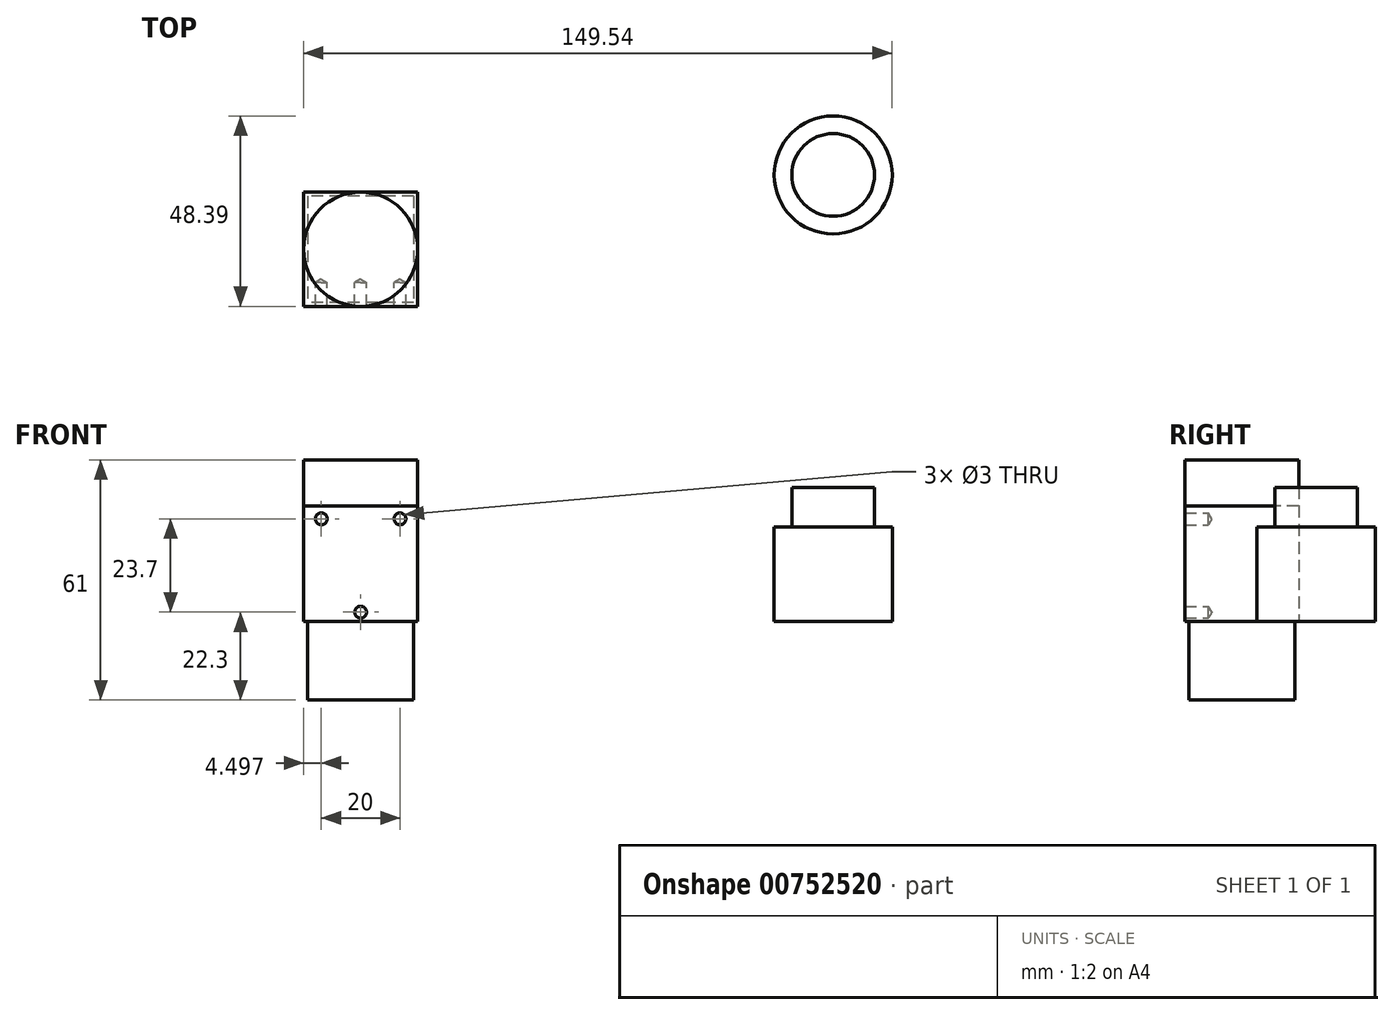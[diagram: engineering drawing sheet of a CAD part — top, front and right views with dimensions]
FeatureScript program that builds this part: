
annotation { "Feature Type Name" : "Feature", "Feature Type Description" : "" }
export const myFeature = defineFeature(function(context is Context, id is Id, definition is map)
    precondition{}
    {
        {
            var Q0;
            Q0=qCreatedBy(makeId("Top.planeOp"),FACE);
            var sketch = newSketch(context, id + "F0", { "sketchPlane" : qUnion([Q0])});
            skLineSegment(sketch, "E0.bottom", {"start": v(-92.76, 40.6) * mm, "end": v(-63.76, 40.6) * mm});
            skLineSegment(sketch, "E0.top", {"start": v(-92.76, 11.6) * mm, "end": v(-63.76, 11.6) * mm});
            skLineSegment(sketch, "E0.left", {"start": v(-92.76, 40.6) * mm, "end": v(-92.76, 11.6) * mm});
            skLineSegment(sketch, "E0.right", {"start": v(-63.76, 40.6) * mm, "end": v(-63.76, 11.6) * mm});
            skCircle(sketch, "E1", {"center": v(41.78, 44.98) * mm, "radius": 15 * mm});
            skCircle(sketch, "E2", {"center": v(41.78, 44.98) * mm, "radius": 10.5 * mm});
            skLineSegment(sketch, "E3", {"start": v(-92.76, 40.6) * mm, "end": v(-63.76, 11.6) * mm, "construction": true});
            skPoint(sketch, "E4", {"position": v(-78.26, 26.1) * mm});
            skCircle(sketch, "E5", {"center": v(-78.26, 26.1) * mm, "radius": 14.5 * mm});
            skLineSegment(sketch, "E6.bottom", {"start": v(-64.76, 39.6) * mm, "end": v(-91.76, 39.6) * mm});
            skLineSegment(sketch, "E6.top", {"start": v(-64.76, 12.6) * mm, "end": v(-91.76, 12.6) * mm});
            skLineSegment(sketch, "E6.left", {"start": v(-64.76, 39.6) * mm, "end": v(-64.76, 12.6) * mm});
            skLineSegment(sketch, "E6.right", {"start": v(-91.76, 39.6) * mm, "end": v(-91.76, 12.6) * mm});
            skSolve(sketch);
        }
        {
            var Q0;
            {var subQ0=sQuery(id+"F0.wireOp",EDGE,"E0.right");var subQ1=sQuery(id+"F0.wireOp",EDGE,"E0.bottom");var subQ2=makeQuery(id+"F0.imprint","INTERSECT",VERTEX,{"derivedFrom":[subQ1,subQ0]});Q0=makeQuery(id+"F0.imprint","IMPRINT",FACE,{"disambiguationData":[TD([[makeQuery(id+"F0.imprint","IMPRINT",EDGE,{"disambiguationData":[TD([[subQ2,1.0]])],"derivedFrom":subQ1}),-1.0]])]});}
            var Q1;
            {var subQ0=sQuery(id+"F0.wireOp",EDGE,"E0.right");var subQ1=sQuery(id+"F0.wireOp",EDGE,"E0.top");var subQ2=makeQuery(id+"F0.imprint","INTERSECT",VERTEX,{"derivedFrom":[subQ1,subQ0]});Q1=makeQuery(id+"F0.imprint","IMPRINT",FACE,{"disambiguationData":[TD([[makeQuery(id+"F0.imprint","IMPRINT",EDGE,{"disambiguationData":[TD([[subQ2,1.0]])],"derivedFrom":subQ1}),1.0]])]});}
            var Q2;
            {var subQ0=sQuery(id+"F0.wireOp",EDGE,"E5");var subQ1=makeQuery(id+"F0.imprint","INTERSECT",VERTEX,{"derivedFrom":[sQuery(id+"F0.wireOp",EDGE,"E0.bottom"),subQ0]});Q2=makeQuery(id+"F0.imprint","IMPRINT",FACE,{"disambiguationData":[TD([[makeQuery(id+"F0.imprint","IMPRINT",EDGE,{"disambiguationData":[TD([[subQ1,1.0]])],"derivedFrom":subQ0}),1.0]])]});}
            var Q3;
            {var subQ0=sQuery(id+"F0.wireOp",EDGE,"E0.left");var subQ1=sQuery(id+"F0.wireOp",EDGE,"E0.bottom");var subQ2=makeQuery(id+"F0.imprint","INTERSECT",VERTEX,{"derivedFrom":[subQ1,subQ0]});Q3=makeQuery(id+"F0.imprint","IMPRINT",FACE,{"disambiguationData":[TD([[makeQuery(id+"F0.imprint","IMPRINT",EDGE,{"disambiguationData":[TD([[subQ2,-1.0]])],"derivedFrom":subQ1}),-1.0]])]});}
            var Q4;
            {var subQ1=sQuery(id+"F0.wireOp",EDGE,"E5");var subQ3=sQuery(id+"F0.wireOp",EDGE,"E6.left");var subQ11=makeQuery(id+"F0.imprint","INTERSECT",VERTEX,{"disambiguationData":[OD(0.0)],"derivedFrom":[subQ1,subQ3]});Q4=makeQuery(id+"F0.imprint","IMPRINT",FACE,{"disambiguationData":[TD([[makeQuery(id+"F0.imprint","IMPRINT",EDGE,{"disambiguationData":[TD([[subQ11,-1.0]])],"derivedFrom":subQ1}),1.0]])]});}
            var Q5;
            {var subQ0=sQuery(id+"F0.wireOp",EDGE,"E6.left");var subQ1=sQuery(id+"F0.wireOp",EDGE,"E5");var subQ2=makeQuery(id+"F0.imprint","INTERSECT",VERTEX,{"disambiguationData":[OD(0.0)],"derivedFrom":[subQ1,subQ0]});Q5=makeQuery(id+"F0.imprint","IMPRINT",FACE,{"disambiguationData":[TD([[makeQuery(id+"F0.imprint","IMPRINT",EDGE,{"disambiguationData":[TD([[subQ2,-1.0]])],"derivedFrom":subQ1}),-1.0]])]});}
            var Q6;
            {var subQ0=sQuery(id+"F0.wireOp",EDGE,"E6.bottom");var subQ1=sQuery(id+"F0.wireOp",EDGE,"E5");var subQ2=makeQuery(id+"F0.imprint","INTERSECT",VERTEX,{"disambiguationData":[OD(1.0)],"derivedFrom":[subQ1,subQ0]});Q6=makeQuery(id+"F0.imprint","IMPRINT",FACE,{"disambiguationData":[TD([[makeQuery(id+"F0.imprint","IMPRINT",EDGE,{"disambiguationData":[TD([[subQ2,-1.0]])],"derivedFrom":subQ1}),-1.0]])]});}
            var Q7;
            {var subQ0=sQuery(id+"F0.wireOp",EDGE,"E6.right");var subQ1=sQuery(id+"F0.wireOp",EDGE,"E5");var subQ2=makeQuery(id+"F0.imprint","INTERSECT",VERTEX,{"disambiguationData":[OD(1.0)],"derivedFrom":[subQ1,subQ0]});Q7=makeQuery(id+"F0.imprint","IMPRINT",FACE,{"disambiguationData":[TD([[makeQuery(id+"F0.imprint","IMPRINT",EDGE,{"disambiguationData":[TD([[subQ2,-1.0]])],"derivedFrom":subQ1}),-1.0]])]});}
            var Q8;
            {var subQ0=sQuery(id+"F0.wireOp",EDGE,"E6.top");var subQ1=sQuery(id+"F0.wireOp",EDGE,"E5");var subQ2=makeQuery(id+"F0.imprint","INTERSECT",VERTEX,{"disambiguationData":[OD(1.0)],"derivedFrom":[subQ1,subQ0]});Q8=makeQuery(id+"F0.imprint","IMPRINT",FACE,{"disambiguationData":[TD([[makeQuery(id+"F0.imprint","IMPRINT",EDGE,{"disambiguationData":[TD([[subQ2,-1.0]])],"derivedFrom":subQ1}),-1.0]])]});}
            var Q9;
            {var subQ0=sQuery(id+"F0.wireOp",EDGE,"E5");var subQ1=makeQuery(id+"F0.imprint","INTERSECT",VERTEX,{"derivedFrom":[sQuery(id+"F0.wireOp",EDGE,"E0.top"),subQ0]});Q9=makeQuery(id+"F0.imprint","IMPRINT",FACE,{"disambiguationData":[TD([[makeQuery(id+"F0.imprint","IMPRINT",EDGE,{"disambiguationData":[TD([[subQ1,1.0]])],"derivedFrom":subQ0}),1.0]])]});}
            var Q10;
            {var subQ1=sQuery(id+"F0.wireOp",EDGE,"E0.top");var subQ5=sQuery(id+"F0.wireOp",EDGE,"E0.left");var subQ9=makeQuery(id+"F0.imprint","INTERSECT",VERTEX,{"derivedFrom":[subQ1,subQ5]});Q10=makeQuery(id+"F0.imprint","IMPRINT",FACE,{"disambiguationData":[TD([[makeQuery(id+"F0.imprint","IMPRINT",EDGE,{"disambiguationData":[TD([[subQ9,-1.0]])],"derivedFrom":subQ1}),1.0]])]});}
            var Q11;
            {var subQ0=sQuery(id+"F0.wireOp",EDGE,"E5");var subQ1=makeQuery(id+"F0.imprint","INTERSECT",VERTEX,{"derivedFrom":[sQuery(id+"F0.wireOp",EDGE,"E0.right"),subQ0]});Q11=makeQuery(id+"F0.imprint","IMPRINT",FACE,{"disambiguationData":[TD([[makeQuery(id+"F0.imprint","IMPRINT",EDGE,{"disambiguationData":[TD([[subQ1,-1.0]])],"derivedFrom":subQ0}),1.0]])]});}
            var Q12;
            {var subQ0=sQuery(id+"F0.wireOp",EDGE,"E5");var subQ1=makeQuery(id+"F0.imprint","INTERSECT",VERTEX,{"derivedFrom":[sQuery(id+"F0.wireOp",EDGE,"E0.left"),subQ0]});Q12=makeQuery(id+"F0.imprint","IMPRINT",FACE,{"disambiguationData":[TD([[makeQuery(id+"F0.imprint","IMPRINT",EDGE,{"disambiguationData":[TD([[subQ1,1.0]])],"derivedFrom":subQ0}),1.0]])]});}
            extrude(context, id + "F1", {"entities" : qUnion([Q0, Q1, Q2, Q3, Q4, Q5, Q6, Q7, Q8, Q9, Q10, Q11, Q12]), "depth" : 29.3 * mm, "offsetDistance" : 25 * mm});
        }
        {
            var Q0;
            {var subQ0=sQuery(id+"F0.wireOp",EDGE,"E5");var subQ1=makeQuery(id+"F0.imprint","INTERSECT",VERTEX,{"derivedFrom":[sQuery(id+"F0.wireOp",EDGE,"E0.bottom"),subQ0]});Q0=makeQuery(id+"F0.imprint","IMPRINT",FACE,{"disambiguationData":[TD([[makeQuery(id+"F0.imprint","IMPRINT",EDGE,{"disambiguationData":[TD([[subQ1,1.0]])],"derivedFrom":subQ0}),1.0]])]});}
            var Q1;
            {var subQ1=sQuery(id+"F0.wireOp",EDGE,"E5");var subQ3=sQuery(id+"F0.wireOp",EDGE,"E6.left");var subQ11=makeQuery(id+"F0.imprint","INTERSECT",VERTEX,{"disambiguationData":[OD(0.0)],"derivedFrom":[subQ1,subQ3]});Q1=makeQuery(id+"F0.imprint","IMPRINT",FACE,{"disambiguationData":[TD([[makeQuery(id+"F0.imprint","IMPRINT",EDGE,{"disambiguationData":[TD([[subQ11,-1.0]])],"derivedFrom":subQ1}),1.0]])]});}
            var Q2;
            {var subQ0=sQuery(id+"F0.wireOp",EDGE,"E5");var subQ1=makeQuery(id+"F0.imprint","INTERSECT",VERTEX,{"derivedFrom":[sQuery(id+"F0.wireOp",EDGE,"E0.left"),subQ0]});Q2=makeQuery(id+"F0.imprint","IMPRINT",FACE,{"disambiguationData":[TD([[makeQuery(id+"F0.imprint","IMPRINT",EDGE,{"disambiguationData":[TD([[subQ1,1.0]])],"derivedFrom":subQ0}),1.0]])]});}
            var Q3;
            {var subQ0=sQuery(id+"F0.wireOp",EDGE,"E5");var subQ1=makeQuery(id+"F0.imprint","INTERSECT",VERTEX,{"derivedFrom":[sQuery(id+"F0.wireOp",EDGE,"E0.top"),subQ0]});Q3=makeQuery(id+"F0.imprint","IMPRINT",FACE,{"disambiguationData":[TD([[makeQuery(id+"F0.imprint","IMPRINT",EDGE,{"disambiguationData":[TD([[subQ1,1.0]])],"derivedFrom":subQ0}),1.0]])]});}
            var Q4;
            {var subQ0=sQuery(id+"F0.wireOp",EDGE,"E5");var subQ1=makeQuery(id+"F0.imprint","INTERSECT",VERTEX,{"derivedFrom":[sQuery(id+"F0.wireOp",EDGE,"E0.right"),subQ0]});Q4=makeQuery(id+"F0.imprint","IMPRINT",FACE,{"disambiguationData":[TD([[makeQuery(id+"F0.imprint","IMPRINT",EDGE,{"disambiguationData":[TD([[subQ1,-1.0]])],"derivedFrom":subQ0}),1.0]])]});}
            extrude(context, id + "F2", {"entities" : qUnion([Q0, Q1, Q2, Q3, Q4]), "operationType" : NewBodyOperationType.ADD, "depth" : 41 * mm, "offsetDistance" : 25 * mm});
        }
        {
            var Q0;
            Q0=makeQuery(id+"F0.imprint","IMPRINT",FACE,{"disambiguationData":[TD([[makeQuery(id+"F0.imprint","IMPRINT",EDGE,{"derivedFrom":sQuery(id+"F0.wireOp",EDGE,"E1")}),1.0]])]});
            var Q1;
            Q1=makeQuery(id+"F0.imprint","IMPRINT",FACE,{"disambiguationData":[TD([[makeQuery(id+"F0.imprint","IMPRINT",EDGE,{"derivedFrom":sQuery(id+"F0.wireOp",EDGE,"E2")}),1.0]])]});
            extrude(context, id + "F3", {"entities" : qUnion([Q0, Q1]), "depth" : 24 * mm, "offsetDistance" : 25 * mm});
        }
        {
            var Q0;
            Q0=makeQuery(id+"F0.imprint","IMPRINT",FACE,{"disambiguationData":[TD([[makeQuery(id+"F0.imprint","IMPRINT",EDGE,{"derivedFrom":sQuery(id+"F0.wireOp",EDGE,"E2")}),1.0]])]});
            extrude(context, id + "F4", {"entities" : qUnion([Q0]), "operationType" : NewBodyOperationType.ADD, "depth" : 34 * mm, "offsetDistance" : 25 * mm});
        }
        {
            var Q0;
            {var subQ1=sQuery(id+"F0.wireOp",EDGE,"E5");var subQ3=sQuery(id+"F0.wireOp",EDGE,"E6.left");var subQ11=makeQuery(id+"F0.imprint","INTERSECT",VERTEX,{"disambiguationData":[OD(0.0)],"derivedFrom":[subQ1,subQ3]});Q0=makeQuery(id+"F0.imprint","IMPRINT",FACE,{"disambiguationData":[TD([[makeQuery(id+"F0.imprint","IMPRINT",EDGE,{"disambiguationData":[TD([[subQ11,-1.0]])],"derivedFrom":subQ1}),1.0]])]});}
            var Q1;
            {var subQ0=sQuery(id+"F0.wireOp",EDGE,"E6.left");var subQ1=sQuery(id+"F0.wireOp",EDGE,"E5");var subQ2=makeQuery(id+"F0.imprint","INTERSECT",VERTEX,{"disambiguationData":[OD(0.0)],"derivedFrom":[subQ1,subQ0]});Q1=makeQuery(id+"F0.imprint","IMPRINT",FACE,{"disambiguationData":[TD([[makeQuery(id+"F0.imprint","IMPRINT",EDGE,{"disambiguationData":[TD([[subQ2,-1.0]])],"derivedFrom":subQ1}),-1.0]])]});}
            var Q2;
            {var subQ0=sQuery(id+"F0.wireOp",EDGE,"E6.bottom");var subQ1=sQuery(id+"F0.wireOp",EDGE,"E5");var subQ2=makeQuery(id+"F0.imprint","INTERSECT",VERTEX,{"disambiguationData":[OD(1.0)],"derivedFrom":[subQ1,subQ0]});Q2=makeQuery(id+"F0.imprint","IMPRINT",FACE,{"disambiguationData":[TD([[makeQuery(id+"F0.imprint","IMPRINT",EDGE,{"disambiguationData":[TD([[subQ2,-1.0]])],"derivedFrom":subQ1}),-1.0]])]});}
            var Q3;
            {var subQ0=sQuery(id+"F0.wireOp",EDGE,"E6.right");var subQ1=sQuery(id+"F0.wireOp",EDGE,"E5");var subQ2=makeQuery(id+"F0.imprint","INTERSECT",VERTEX,{"disambiguationData":[OD(1.0)],"derivedFrom":[subQ1,subQ0]});Q3=makeQuery(id+"F0.imprint","IMPRINT",FACE,{"disambiguationData":[TD([[makeQuery(id+"F0.imprint","IMPRINT",EDGE,{"disambiguationData":[TD([[subQ2,-1.0]])],"derivedFrom":subQ1}),-1.0]])]});}
            var Q4;
            {var subQ0=sQuery(id+"F0.wireOp",EDGE,"E6.top");var subQ1=sQuery(id+"F0.wireOp",EDGE,"E5");var subQ2=makeQuery(id+"F0.imprint","INTERSECT",VERTEX,{"disambiguationData":[OD(1.0)],"derivedFrom":[subQ1,subQ0]});Q4=makeQuery(id+"F0.imprint","IMPRINT",FACE,{"disambiguationData":[TD([[makeQuery(id+"F0.imprint","IMPRINT",EDGE,{"disambiguationData":[TD([[subQ2,-1.0]])],"derivedFrom":subQ1}),-1.0]])]});}
            extrude(context, id + "F5", {"entities" : qUnion([Q0, Q1, Q2, Q3, Q4]), "operationType" : NewBodyOperationType.ADD, "oppositeDirection" : true, "depth" : 20 * mm, "offsetDistance" : 25 * mm});
        }
        {
            var Q0;
            Q0=makeQuery(id+"F1.opExtrude","SWEPT_FACE",FACE,{"disambiguationData":[OSD([sQuery(id+"F0.wireOp",EDGE,"E0.top")])]});
            var sketch = newSketch(context, id + "F6", { "sketchPlane" : qUnion([Q0])});
            skPoint(sketch, "E7", {"position": v(-68.26, 26) * mm});
            skPoint(sketch, "E8", {"position": v(-88.26, 26) * mm});
            skLineSegment(sketch, "E9", {"start": v(-78.26, 29.3) * mm, "end": v(-78.26, 0) * mm, "construction": true});
            skPoint(sketch, "E10", {"position": v(-78.26, 2.3) * mm});
            skSolve(sketch);
        }
        {
            var Q0;
            Q0=sQuery(id+"F6.wireOp",VERTEX,"E7");
            var Q1;
            Q1=sQuery(id+"F6.wireOp",VERTEX,"E10");
            var Q2;
            Q2=sQuery(id+"F6.wireOp",VERTEX,"E8");
            var Q3;
            Q3=makeQuery(id+"F1.opExtrude","SWEPT_BODY",BODY,{"disambiguationData":[OSD([sQuery(id+"F0.wireOp",EDGE,"E0.bottom"),sQuery(id+"F0.wireOp",EDGE,"E0.top"),sQuery(id+"F0.wireOp",EDGE,"E0.left"),sQuery(id+"F0.wireOp",EDGE,"E0.right")])]});
            hole(context, id + "F7", {"style" : HoleStyle.SIMPLE, "endStyle" : HoleEndStyle.BLIND, "holeDiameter" : 3 * mm, "majorDiameter" : 5 * mm, "holeDepth" : 6 * mm, "isTappedThrough" : true, "tappedDepth" : 12 * mm, "tapClearance" : 3, "locations" : qUnion([Q0, Q1, Q2]), "scope" : qUnion([Q3]), "startStyle" : HoleStartStyle.PART});
        }
    });
